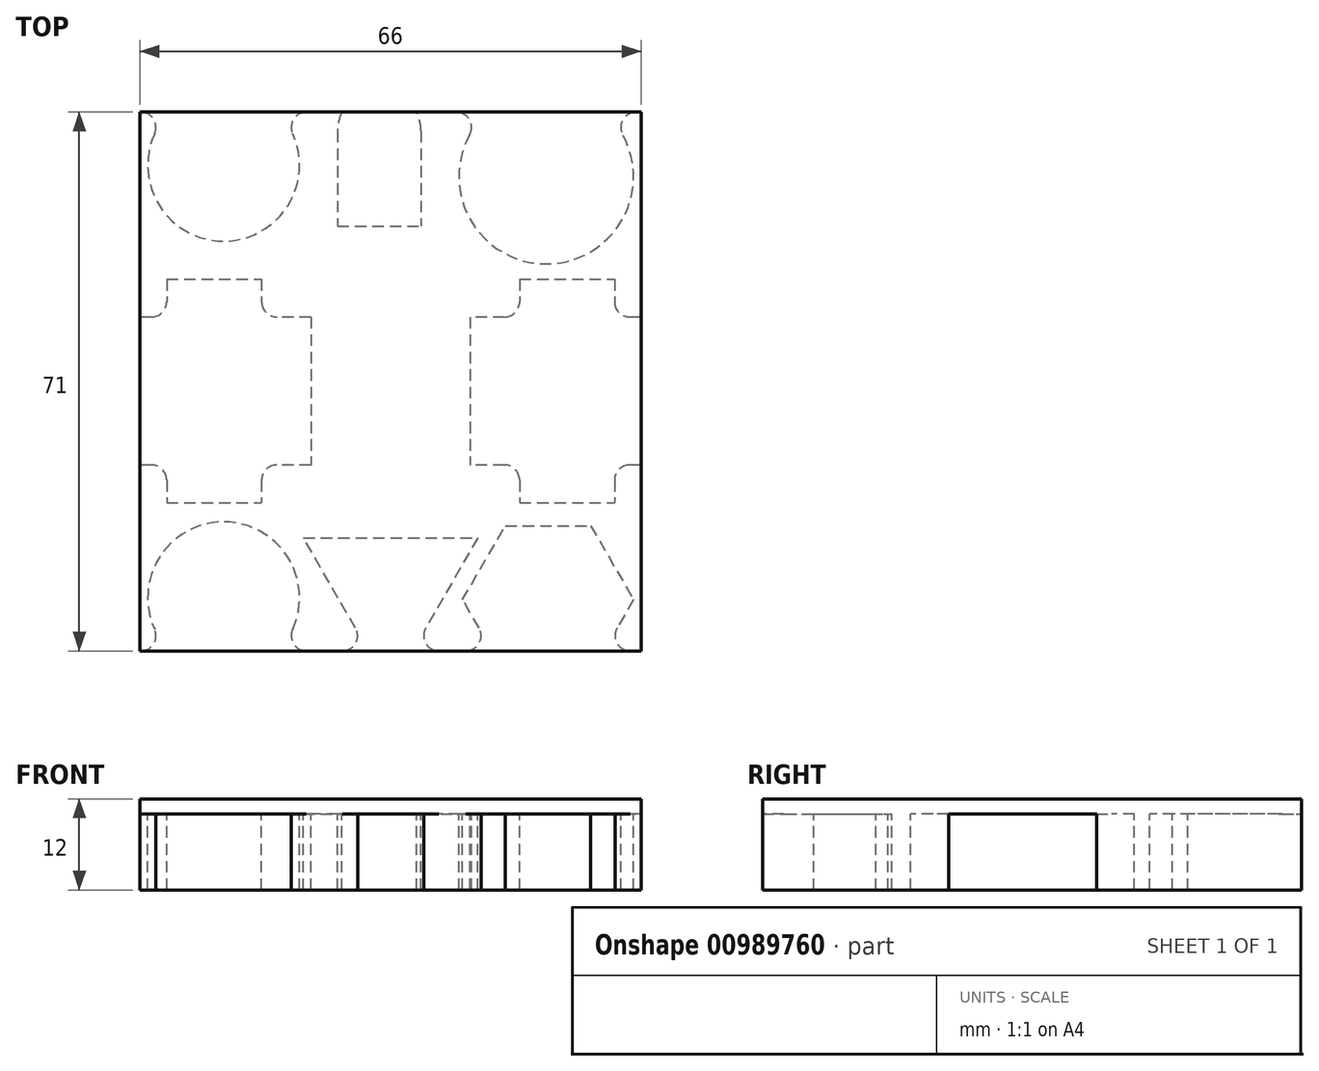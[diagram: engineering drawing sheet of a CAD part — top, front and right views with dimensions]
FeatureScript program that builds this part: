
annotation { "Feature Type Name" : "Feature", "Feature Type Description" : "" }
export const myFeature = defineFeature(function(context is Context, id is Id, definition is map)
    precondition{}
    {
        {
            assignVariable(context, id + "F0", {"name" : "extrude", "anyValue" : 10});
        }
        {
            var Q0;
            Q0=qCreatedBy(makeId("Top.planeOp"),FACE);
            var sketch = newSketch(context, id + "F1", { "sketchPlane" : qUnion([Q0])});
            skLineSegment(sketch, "E0.bottom", {"start": v(-33, 35.5) * mm, "end": v(33, 35.5) * mm});
            skLineSegment(sketch, "E0.top", {"start": v(-33, -35.5) * mm, "end": v(33, -35.5) * mm});
            skLineSegment(sketch, "E0.left", {"start": v(-33, 35.5) * mm, "end": v(-33, -35.5) * mm});
            skLineSegment(sketch, "E0.right", {"start": v(33, 35.5) * mm, "end": v(33, -35.5) * mm});
            skCircle(sketch, "E1", {"center": v(-22, 28.5) * mm, "radius": 10 * mm});
            skCircle(sketch, "E2", {"center": v(-22, -28.5) * mm, "radius": 10 * mm});
            skCircle(sketch, "E3", {"center": v(20.5, 27) * mm, "radius": 11.5 * mm});
            skCircle(sketch, "E4", {"center": v(-1.5, 33) * mm, "radius": 5.5 * mm});
            skLineSegment(sketch, "E5.bottom", {"start": v(-7, 33) * mm, "end": v(4, 33) * mm});
            skLineSegment(sketch, "E5.top", {"start": v(-7, 20.5) * mm, "end": v(4, 20.5) * mm});
            skLineSegment(sketch, "E5.left", {"start": v(-7, 33) * mm, "end": v(-7, 20.5) * mm});
            skLineSegment(sketch, "E5.right", {"start": v(4, 33) * mm, "end": v(4, 20.5) * mm});
            skLineSegment(sketch, "E6.bottom", {"start": v(-36, 38.5) * mm, "end": v(36, 38.5) * mm});
            skLineSegment(sketch, "E6.top", {"start": v(-36, -38.5) * mm, "end": v(36, -38.5) * mm});
            skLineSegment(sketch, "E6.left", {"start": v(-36, 38.5) * mm, "end": v(-36, -38.5) * mm});
            skLineSegment(sketch, "E6.right", {"start": v(36, 38.5) * mm, "end": v(36, -38.5) * mm});
            skCircle(sketch, "E7.cCircle", {"center": v(0, -27.22) * mm, "radius": 6.64 * mm, "construction": true});
            skLineSegment(sketch, "E7.0", {"start": v(11.5, -20.58) * mm, "end": v(0, -40.5) * mm});
            skLineSegment(sketch, "E7.1", {"start": v(0, -40.5) * mm, "end": v(-11.5, -20.58) * mm});
            skLineSegment(sketch, "E7.2", {"start": v(-11.5, -20.58) * mm, "end": v(11.5, -20.58) * mm});
            skPoint(sketch, "E7.0.midPoint", {"position": v(5.75, -30.54) * mm});
            skLineSegment(sketch, "E8.bottom", {"start": v(-222.38, 29.41) * mm, "end": v(-222.38, -0.09) * mm});
            skLineSegment(sketch, "E8.top", {"start": v(-209.88, 29.41) * mm, "end": v(-209.88, -0.09) * mm});
            skLineSegment(sketch, "E8.left", {"start": v(-222.38, 29.41) * mm, "end": v(-209.88, 29.41) * mm});
            skLineSegment(sketch, "E8.right", {"start": v(-222.38, -0.09) * mm, "end": v(-209.88, -0.09) * mm});
            skLineSegment(sketch, "E9.bottom", {"start": v(-203.38, 24.41) * mm, "end": v(-203.38, 4.91) * mm});
            skLineSegment(sketch, "E9.top", {"start": v(-228.88, 24.41) * mm, "end": v(-228.88, 4.91) * mm});
            skLineSegment(sketch, "E9.left", {"start": v(-203.38, 24.41) * mm, "end": v(-228.88, 24.41) * mm});
            skLineSegment(sketch, "E9.right", {"start": v(-203.38, 4.91) * mm, "end": v(-228.88, 4.91) * mm});
            skLineSegment(sketch, "E10", {"start": v(-228.88, 14.66) * mm, "end": v(-203.38, 14.66) * mm, "construction": true});
            skLineSegment(sketch, "E11", {"start": v(-216.13, -0.09) * mm, "end": v(-216.13, 29.41) * mm, "construction": true});
            skLineSegment(sketch, "E12.bottom", {"start": v(-29.5, 13.5) * mm, "end": v(-29.5, -16) * mm});
            skLineSegment(sketch, "E12.top", {"start": v(-17, 13.5) * mm, "end": v(-17, -16) * mm});
            skLineSegment(sketch, "E12.left", {"start": v(-29.5, 13.5) * mm, "end": v(-17, 13.5) * mm});
            skLineSegment(sketch, "E12.right", {"start": v(-29.5, -16) * mm, "end": v(-17, -16) * mm});
            skLineSegment(sketch, "E13.bottom", {"start": v(-10.5, 8.5) * mm, "end": v(-10.5, -11) * mm});
            skLineSegment(sketch, "E13.top", {"start": v(-36, 8.5) * mm, "end": v(-36, -11) * mm});
            skLineSegment(sketch, "E13.left", {"start": v(-10.5, 8.5) * mm, "end": v(-36, 8.5) * mm});
            skLineSegment(sketch, "E13.right", {"start": v(-10.5, -11) * mm, "end": v(-36, -11) * mm});
            skLineSegment(sketch, "E14", {"start": v(-36, -1.25) * mm, "end": v(-10.5, -1.25) * mm, "construction": true});
            skLineSegment(sketch, "E15", {"start": v(-23.25, -16) * mm, "end": v(-23.25, 13.5) * mm, "construction": true});
            skLineSegment(sketch, "E16.bottom", {"start": v(17, 13.5) * mm, "end": v(17, -16) * mm});
            skLineSegment(sketch, "E16.top", {"start": v(29.5, 13.5) * mm, "end": v(29.5, -16) * mm});
            skLineSegment(sketch, "E16.left", {"start": v(17, 13.5) * mm, "end": v(29.5, 13.5) * mm});
            skLineSegment(sketch, "E16.right", {"start": v(17, -16) * mm, "end": v(29.5, -16) * mm});
            skLineSegment(sketch, "E17.bottom", {"start": v(36, 8.5) * mm, "end": v(36, -11) * mm});
            skLineSegment(sketch, "E17.top", {"start": v(10.5, 8.5) * mm, "end": v(10.5, -11) * mm});
            skLineSegment(sketch, "E17.left", {"start": v(36, 8.5) * mm, "end": v(10.5, 8.5) * mm});
            skLineSegment(sketch, "E17.right", {"start": v(36, -11) * mm, "end": v(10.5, -11) * mm});
            skLineSegment(sketch, "E18", {"start": v(10.5, -1.25) * mm, "end": v(36, -1.25) * mm, "construction": true});
            skLineSegment(sketch, "E19", {"start": v(23.25, -16) * mm, "end": v(23.25, 13.5) * mm, "construction": true});
            skCircle(sketch, "E20.cCircle", {"center": v(20.74, -28.75) * mm, "radius": 9.75 * mm, "construction": true});
            skLineSegment(sketch, "E20.0", {"start": v(26.37, -38.5) * mm, "end": v(15.11, -38.5) * mm});
            skLineSegment(sketch, "E20.1", {"start": v(15.11, -38.5) * mm, "end": v(9.48, -28.75) * mm});
            skLineSegment(sketch, "E20.2", {"start": v(9.48, -28.75) * mm, "end": v(15.11, -19) * mm});
            skLineSegment(sketch, "E20.3", {"start": v(15.11, -19) * mm, "end": v(26.37, -19) * mm});
            skLineSegment(sketch, "E20.4", {"start": v(26.37, -19) * mm, "end": v(32, -28.75) * mm});
            skLineSegment(sketch, "E20.5", {"start": v(32, -28.75) * mm, "end": v(26.37, -38.5) * mm});
            skPoint(sketch, "E20.0.midPoint", {"position": v(20.74, -38.5) * mm});
            skSolve(sketch);
        }
        {
            var Q0;
            {var subQ25=sQuery(id+"F1.wireOp",EDGE,"E0.left");Q0=makeQuery(id+"F1.imprint","IMPRINT",FACE,{"disambiguationData":[TD([[makeQuery(id+"F1.imprint","IMPRINT",EDGE,{"derivedFrom":subQ25}),1.0]])]});}
            var Q1;
            {var subQ0=sQuery(id+"F1.wireOp",EDGE,"E1");var subQ1=sQuery(id+"F1.wireOp",EDGE,"E0.bottom");var subQ2=makeQuery(id+"F1.imprint","INTERSECT",VERTEX,{"disambiguationData":[OD(0.0)],"derivedFrom":[subQ1,subQ0]});Q1=makeQuery(id+"F1.imprint","IMPRINT",FACE,{"disambiguationData":[TD([[makeQuery(id+"F1.imprint","IMPRINT",EDGE,{"disambiguationData":[TD([[subQ2,-1.0]])],"derivedFrom":subQ1}),-1.0]])]});}
            var Q2;
            Q2=makeQuery(id+"F1.imprint","IMPRINT",FACE,{"disambiguationData":[TD([[makeQuery(id+"F1.imprint","IMPRINT",EDGE,{"derivedFrom":sQuery(id+"F1.wireOp",EDGE,"RRiEwcH1-bZLO-szws-cHMA-7Pnru7wUDrEX.bottom")}),-1.0]])]});
            var Q3;
            Q3=makeQuery(id+"F1.imprint","IMPRINT",FACE,{"disambiguationData":[TD([[makeQuery(id+"F1.imprint","IMPRINT",EDGE,{"derivedFrom":sQuery(id+"F1.wireOp",EDGE,"i1Ranwmf-v3kT-W1ZZ-sd1X-YmdqdP5lJLtx.bottom")}),-1.0]])]});
            var Q4;
            {var subQ0=sQuery(id+"F1.wireOp",EDGE,"E2");var subQ1=sQuery(id+"F1.wireOp",EDGE,"E0.top");var subQ2=makeQuery(id+"F1.imprint","INTERSECT",VERTEX,{"disambiguationData":[OD(0.0)],"derivedFrom":[subQ1,subQ0]});Q4=makeQuery(id+"F1.imprint","IMPRINT",FACE,{"disambiguationData":[TD([[makeQuery(id+"F1.imprint","IMPRINT",EDGE,{"disambiguationData":[TD([[subQ2,-1.0]])],"derivedFrom":subQ1}),1.0]])]});}
            var Q5;
            {var subQ5=sQuery(id+"F1.wireOp",EDGE,"E7.2");Q5=makeQuery(id+"F1.imprint","IMPRINT",FACE,{"disambiguationData":[TD([[makeQuery(id+"F1.imprint","IMPRINT",EDGE,{"derivedFrom":subQ5}),-1.0]])]});}
            var Q6;
            {var subQ0=sQuery(id+"F1.wireOp",EDGE,"E3");var subQ1=sQuery(id+"F1.wireOp",EDGE,"E0.bottom");var subQ2=makeQuery(id+"F1.imprint","INTERSECT",VERTEX,{"disambiguationData":[OD(0.0)],"derivedFrom":[subQ1,subQ0]});Q6=makeQuery(id+"F1.imprint","IMPRINT",FACE,{"disambiguationData":[TD([[makeQuery(id+"F1.imprint","IMPRINT",EDGE,{"disambiguationData":[TD([[subQ2,-1.0]])],"derivedFrom":subQ1}),-1.0]])]});}
            var Q7;
            {var subQ5=sQuery(id+"F1.wireOp",EDGE,"fb6c445c-8afe-4bf9-a477-5b88ef33b572.0");Q7=makeQuery(id+"F1.imprint","IMPRINT",FACE,{"disambiguationData":[TD([[makeQuery(id+"F1.imprint","IMPRINT",EDGE,{"derivedFrom":subQ5}),-1.0]])]});}
            var Q8;
            Q8=makeQuery(id+"F1.imprint","IMPRINT",FACE,{"disambiguationData":[TD([[makeQuery(id+"F1.imprint","IMPRINT",EDGE,{"derivedFrom":sQuery(id+"F1.wireOp",EDGE,"E5.top")}),-1.0]])]});
            var Q9;
            {var subQ0=sQuery(id+"F1.wireOp",EDGE,"E5.bottom");Q9=makeQuery(id+"F1.imprint","IMPRINT",FACE,{"disambiguationData":[TD([[makeQuery(id+"F1.imprint","IMPRINT",EDGE,{"derivedFrom":subQ0}),1.0]])]});}
            var Q10;
            {var subQ4=sQuery(id+"F1.wireOp",EDGE,"E5.bottom");Q10=makeQuery(id+"F1.imprint","IMPRINT",FACE,{"disambiguationData":[TD([[makeQuery(id+"F1.imprint","IMPRINT",EDGE,{"derivedFrom":subQ4}),-1.0]])]});}
            var Q11;
            Q11=makeQuery(id+"F1.imprint","IMPRINT",FACE,{"disambiguationData":[TD([[makeQuery(id+"F1.imprint","IMPRINT",EDGE,{"derivedFrom":sQuery(id+"F1.wireOp",EDGE,"E5.top")}),1.0]])]});
            var Q12;
            {var subQ5=sQuery(id+"F1.wireOp",EDGE,"E17.top");Q12=makeQuery(id+"F1.imprint","IMPRINT",FACE,{"disambiguationData":[TD([[makeQuery(id+"F1.imprint","IMPRINT",EDGE,{"derivedFrom":subQ5}),1.0]])]});}
            var Q13;
            {var subQ0=sQuery(id+"F1.wireOp",EDGE,"E16.left");Q13=makeQuery(id+"F1.imprint","IMPRINT",FACE,{"disambiguationData":[TD([[makeQuery(id+"F1.imprint","IMPRINT",EDGE,{"derivedFrom":subQ0}),-1.0]])]});}
            var Q14;
            {var subQ0=sQuery(id+"F1.wireOp",EDGE,"E17.left");var subQ1=sQuery(id+"F1.wireOp",EDGE,"E16.bottom");var subQ2=makeQuery(id+"F1.imprint","INTERSECT",VERTEX,{"derivedFrom":[subQ1,subQ0]});Q14=makeQuery(id+"F1.imprint","IMPRINT",FACE,{"disambiguationData":[TD([[makeQuery(id+"F1.imprint","IMPRINT",EDGE,{"disambiguationData":[TD([[subQ2,-1.0]])],"derivedFrom":subQ1}),1.0]])]});}
            var Q15;
            {var subQ0=sQuery(id+"F1.wireOp",EDGE,"E16.right");Q15=makeQuery(id+"F1.imprint","IMPRINT",FACE,{"disambiguationData":[TD([[makeQuery(id+"F1.imprint","IMPRINT",EDGE,{"derivedFrom":subQ0}),1.0]])]});}
            var Q16;
            {var subQ0=sQuery(id+"F1.wireOp",EDGE,"E20.2");Q16=makeQuery(id+"F1.imprint","IMPRINT",FACE,{"disambiguationData":[TD([[makeQuery(id+"F1.imprint","IMPRINT",EDGE,{"derivedFrom":subQ0}),-1.0]])]});}
            var Q17;
            {var subQ0=sQuery(id+"F1.wireOp",EDGE,"E17.left");var subQ1=sQuery(id+"F1.wireOp",EDGE,"E0.right");var subQ2=makeQuery(id+"F1.imprint","INTERSECT",VERTEX,{"derivedFrom":[subQ1,subQ0]});Q17=makeQuery(id+"F1.imprint","IMPRINT",FACE,{"disambiguationData":[TD([[makeQuery(id+"F1.imprint","IMPRINT",EDGE,{"disambiguationData":[TD([[subQ2,-1.0]])],"derivedFrom":subQ1}),-1.0]])]});}
            var Q18;
            {var subQ0=sQuery(id+"F1.wireOp",EDGE,"E13.left");var subQ1=sQuery(id+"F1.wireOp",EDGE,"E0.left");var subQ2=makeQuery(id+"F1.imprint","INTERSECT",VERTEX,{"derivedFrom":[subQ1,subQ0]});Q18=makeQuery(id+"F1.imprint","IMPRINT",FACE,{"disambiguationData":[TD([[makeQuery(id+"F1.imprint","IMPRINT",EDGE,{"disambiguationData":[TD([[subQ2,-1.0]])],"derivedFrom":subQ1}),1.0]])]});}
            var Q19;
            {var subQ0=sQuery(id+"F1.wireOp",EDGE,"E13.left");var subQ1=sQuery(id+"F1.wireOp",EDGE,"E12.bottom");var subQ2=makeQuery(id+"F1.imprint","INTERSECT",VERTEX,{"derivedFrom":[subQ1,subQ0]});Q19=makeQuery(id+"F1.imprint","IMPRINT",FACE,{"disambiguationData":[TD([[makeQuery(id+"F1.imprint","IMPRINT",EDGE,{"disambiguationData":[TD([[subQ2,-1.0]])],"derivedFrom":subQ1}),1.0]])]});}
            var Q20;
            {var subQ5=sQuery(id+"F1.wireOp",EDGE,"E13.bottom");Q20=makeQuery(id+"F1.imprint","IMPRINT",FACE,{"disambiguationData":[TD([[makeQuery(id+"F1.imprint","IMPRINT",EDGE,{"derivedFrom":subQ5}),-1.0]])]});}
            var Q21;
            {var subQ0=sQuery(id+"F1.wireOp",EDGE,"E12.left");Q21=makeQuery(id+"F1.imprint","IMPRINT",FACE,{"disambiguationData":[TD([[makeQuery(id+"F1.imprint","IMPRINT",EDGE,{"derivedFrom":subQ0}),-1.0]])]});}
            var Q22;
            {var subQ0=sQuery(id+"F1.wireOp",EDGE,"E12.right");Q22=makeQuery(id+"F1.imprint","IMPRINT",FACE,{"disambiguationData":[TD([[makeQuery(id+"F1.imprint","IMPRINT",EDGE,{"derivedFrom":subQ0}),1.0]])]});}
            var Q23;
            {var subQ0=sQuery(id+"F1.wireOp",EDGE,"E0.right");var subQ1=sQuery(id+"F1.wireOp",EDGE,"E0.top");var subQ2=makeQuery(id+"F1.imprint","INTERSECT",VERTEX,{"derivedFrom":[subQ1,subQ0]});Q23=makeQuery(id+"F1.imprint","IMPRINT",FACE,{"disambiguationData":[TD([[makeQuery(id+"F1.imprint","IMPRINT",EDGE,{"disambiguationData":[TD([[subQ2,1.0]])],"derivedFrom":subQ1}),1.0]])]});}
            var Q24;
            {var subQ0=sQuery(id+"F1.wireOp",EDGE,"E0.right");var subQ1=sQuery(id+"F1.wireOp",EDGE,"E0.bottom");var subQ2=makeQuery(id+"F1.imprint","INTERSECT",VERTEX,{"derivedFrom":[subQ1,subQ0]});Q24=makeQuery(id+"F1.imprint","IMPRINT",FACE,{"disambiguationData":[TD([[makeQuery(id+"F1.imprint","IMPRINT",EDGE,{"disambiguationData":[TD([[subQ2,1.0]])],"derivedFrom":subQ1}),-1.0]])]});}
            extrude(context, id + "F2", {"entities" : qUnion([Q0, Q1, Q2, Q3, Q4, Q5, Q6, Q7, Q8, Q9, Q10, Q11, Q12, Q13, Q14, Q15, Q16, Q17, Q18, Q19, Q20, Q21, Q22, Q23, Q24]), "depth" : 2 * mm, "offsetDistance" : 25 * mm});
        }
        {
            var Q0;
            Q0=makeQuery(id+"F1.imprint","IMPRINT",FACE,{"disambiguationData":[TD([[makeQuery(id+"F1.imprint","IMPRINT",EDGE,{"derivedFrom":sQuery(id+"F1.wireOp",EDGE,"E5.top")}),-1.0]])]});
            var Q1;
            {var subQ0=sQuery(id+"F1.wireOp",EDGE,"E0.left");var subQ1=sQuery(id+"F1.wireOp",EDGE,"E0.bottom");var subQ2=makeQuery(id+"F1.imprint","INTERSECT",VERTEX,{"derivedFrom":[subQ1,subQ0]});Q1=makeQuery(id+"F1.imprint","IMPRINT",FACE,{"disambiguationData":[TD([[makeQuery(id+"F1.imprint","IMPRINT",EDGE,{"disambiguationData":[TD([[subQ2,-1.0]])],"derivedFrom":subQ1}),-1.0]])]});}
            var Q2;
            {var subQ0=sQuery(id+"F1.wireOp",EDGE,"E0.right");var subQ1=sQuery(id+"F1.wireOp",EDGE,"E0.bottom");var subQ2=makeQuery(id+"F1.imprint","INTERSECT",VERTEX,{"derivedFrom":[subQ1,subQ0]});Q2=makeQuery(id+"F1.imprint","IMPRINT",FACE,{"disambiguationData":[TD([[makeQuery(id+"F1.imprint","IMPRINT",EDGE,{"disambiguationData":[TD([[subQ2,1.0]])],"derivedFrom":subQ1}),-1.0]])]});}
            var Q3;
            {var subQ0=sQuery(id+"F1.wireOp",EDGE,"E0.right");var subQ1=sQuery(id+"F1.wireOp",EDGE,"E0.top");var subQ2=makeQuery(id+"F1.imprint","INTERSECT",VERTEX,{"derivedFrom":[subQ1,subQ0]});Q3=makeQuery(id+"F1.imprint","IMPRINT",FACE,{"disambiguationData":[TD([[makeQuery(id+"F1.imprint","IMPRINT",EDGE,{"disambiguationData":[TD([[subQ2,1.0]])],"derivedFrom":subQ1}),1.0]])]});}
            var Q4;
            {var subQ0=sQuery(id+"F1.wireOp",EDGE,"E0.left");var subQ1=sQuery(id+"F1.wireOp",EDGE,"E0.top");var subQ2=makeQuery(id+"F1.imprint","INTERSECT",VERTEX,{"derivedFrom":[subQ1,subQ0]});Q4=makeQuery(id+"F1.imprint","IMPRINT",FACE,{"disambiguationData":[TD([[makeQuery(id+"F1.imprint","IMPRINT",EDGE,{"disambiguationData":[TD([[subQ2,-1.0]])],"derivedFrom":subQ1}),1.0]])]});}
            extrude(context, id + "F3", {"entities" : qUnion([Q0, Q1, Q2, Q3, Q4]), "operationType" : NewBodyOperationType.ADD, "oppositeDirection" : true, "depth" : (getVariable(context, 'extrude')) * mm, "offsetDistance" : 25 * mm});
        }
        {
            var Q0;
            Q0=makeQuery(id+"F3.opExtrude","SWEPT_EDGE",EDGE,{"disambiguationData":[OSD([sQuery(id+"F1.wireOp",EDGE,"E12.bottom"),sQuery(id+"F1.wireOp",EDGE,"E13.right")])]});
            var Q1;
            Q1=makeQuery(id+"F3.opExtrude","SWEPT_EDGE",EDGE,{"disambiguationData":[OSD([sQuery(id+"F1.wireOp",EDGE,"E12.bottom"),sQuery(id+"F1.wireOp",EDGE,"E13.left")])]});
            var Q2;
            Q2=makeQuery(id+"F3.opExtrude","SWEPT_EDGE",EDGE,{"disambiguationData":[OSD([sQuery(id+"F1.wireOp",EDGE,"E12.top"),sQuery(id+"F1.wireOp",EDGE,"E13.right")])]});
            var Q3;
            Q3=makeQuery(id+"F3.opExtrude","SWEPT_EDGE",EDGE,{"disambiguationData":[OSD([sQuery(id+"F1.wireOp",EDGE,"E12.top"),sQuery(id+"F1.wireOp",EDGE,"E13.left")])]});
            var Q4;
            Q4=makeQuery(id+"F3.opExtrude","SWEPT_EDGE",EDGE,{"disambiguationData":[OSD([sQuery(id+"F1.wireOp",EDGE,"E16.bottom"),sQuery(id+"F1.wireOp",EDGE,"E17.right")])]});
            var Q5;
            Q5=makeQuery(id+"F3.opExtrude","SWEPT_EDGE",EDGE,{"disambiguationData":[OSD([sQuery(id+"F1.wireOp",EDGE,"E16.bottom"),sQuery(id+"F1.wireOp",EDGE,"E17.left")])]});
            var Q6;
            Q6=makeQuery(id+"F3.opExtrude","SWEPT_EDGE",EDGE,{"disambiguationData":[OSD([sQuery(id+"F1.wireOp",EDGE,"E16.top"),sQuery(id+"F1.wireOp",EDGE,"E17.right")])]});
            var Q7;
            Q7=makeQuery(id+"F3.opExtrude","SWEPT_EDGE",EDGE,{"disambiguationData":[OSD([sQuery(id+"F1.wireOp",EDGE,"E16.top"),sQuery(id+"F1.wireOp",EDGE,"E17.left")])]});
            var Q8;
            Q8=makeQuery(id+"F3.opExtrude","SWEPT_EDGE",EDGE,{"disambiguationData":[OSD([sQuery(id+"F1.wireOp",EDGE,"E0.top"),sQuery(id+"F1.wireOp",EDGE,"E7.1")])]});
            var Q9;
            Q9=makeQuery(id+"F3.opExtrude","SWEPT_EDGE",EDGE,{"disambiguationData":[OSD([sQuery(id+"F1.wireOp",EDGE,"E0.top"),sQuery(id+"F1.wireOp",EDGE,"E7.0")])]});
            var Q10;
            {var subQ0=sQuery(id+"F1.wireOp",EDGE,"E3");var subQ1=sQuery(id+"F1.wireOp",EDGE,"E0.bottom");Q10=makeQuery(id+"F3.opExtrude","SWEPT_EDGE",EDGE,{"disambiguationData":[OSD([subQ1,subQ0]),TDD([makeQuery(id+"F1.imprint","INTERSECT",VERTEX,{"disambiguationData":[OD(0.0)],"derivedFrom":[subQ1,subQ0]})])]});}
            var Q11;
            {var subQ0=sQuery(id+"F1.wireOp",EDGE,"E3");var subQ1=sQuery(id+"F1.wireOp",EDGE,"E0.bottom");Q11=makeQuery(id+"F3.opExtrude","SWEPT_EDGE",EDGE,{"disambiguationData":[OSD([subQ1,subQ0]),TDD([makeQuery(id+"F1.imprint","INTERSECT",VERTEX,{"disambiguationData":[OD(1.0)],"derivedFrom":[subQ1,subQ0]})])]});}
            var Q12;
            {var subQ0=sQuery(id+"F1.wireOp",EDGE,"E1");var subQ1=sQuery(id+"F1.wireOp",EDGE,"E0.bottom");Q12=makeQuery(id+"F3.opExtrude","SWEPT_EDGE",EDGE,{"disambiguationData":[OSD([subQ1,subQ0]),TDD([makeQuery(id+"F1.imprint","INTERSECT",VERTEX,{"disambiguationData":[OD(0.0)],"derivedFrom":[subQ1,subQ0]})])]});}
            var Q13;
            {var subQ0=sQuery(id+"F1.wireOp",EDGE,"E1");var subQ1=sQuery(id+"F1.wireOp",EDGE,"E0.bottom");Q13=makeQuery(id+"F3.opExtrude","SWEPT_EDGE",EDGE,{"disambiguationData":[OSD([subQ1,subQ0]),TDD([makeQuery(id+"F1.imprint","INTERSECT",VERTEX,{"disambiguationData":[OD(1.0)],"derivedFrom":[subQ1,subQ0]})])]});}
            var Q14;
            {var subQ0=sQuery(id+"F1.wireOp",EDGE,"E2");var subQ1=sQuery(id+"F1.wireOp",EDGE,"E0.top");Q14=makeQuery(id+"F3.opExtrude","SWEPT_EDGE",EDGE,{"disambiguationData":[OSD([subQ1,subQ0]),TDD([makeQuery(id+"F1.imprint","INTERSECT",VERTEX,{"disambiguationData":[OD(0.0)],"derivedFrom":[subQ1,subQ0]})])]});}
            var Q15;
            {var subQ0=sQuery(id+"F1.wireOp",EDGE,"E2");var subQ1=sQuery(id+"F1.wireOp",EDGE,"E0.top");Q15=makeQuery(id+"F3.opExtrude","SWEPT_EDGE",EDGE,{"disambiguationData":[OSD([subQ1,subQ0]),TDD([makeQuery(id+"F1.imprint","INTERSECT",VERTEX,{"disambiguationData":[OD(1.0)],"derivedFrom":[subQ1,subQ0]})])]});}
            var Q16;
            Q16=makeQuery(id+"F3.opExtrude","SWEPT_EDGE",EDGE,{"disambiguationData":[OSD([sQuery(id+"F1.wireOp",EDGE,"E0.top"),sQuery(id+"F1.wireOp",EDGE,"E20.1")])]});
            var Q17;
            Q17=makeQuery(id+"F3.opExtrude","SWEPT_EDGE",EDGE,{"disambiguationData":[OSD([sQuery(id+"F1.wireOp",EDGE,"E0.top"),sQuery(id+"F1.wireOp",EDGE,"E20.5")])]});
            fillet(context, id + "F4", {"entities" : qUnion([Q0, Q1, Q2, Q3, Q4, Q5, Q6, Q7, Q8, Q9, Q10, Q11, Q12, Q13, Q14, Q15, Q16, Q17]), "radius" : 2 * mm, "tangentPropagation" : true, "allowEdgeOverflow" : false});
        }
    });
